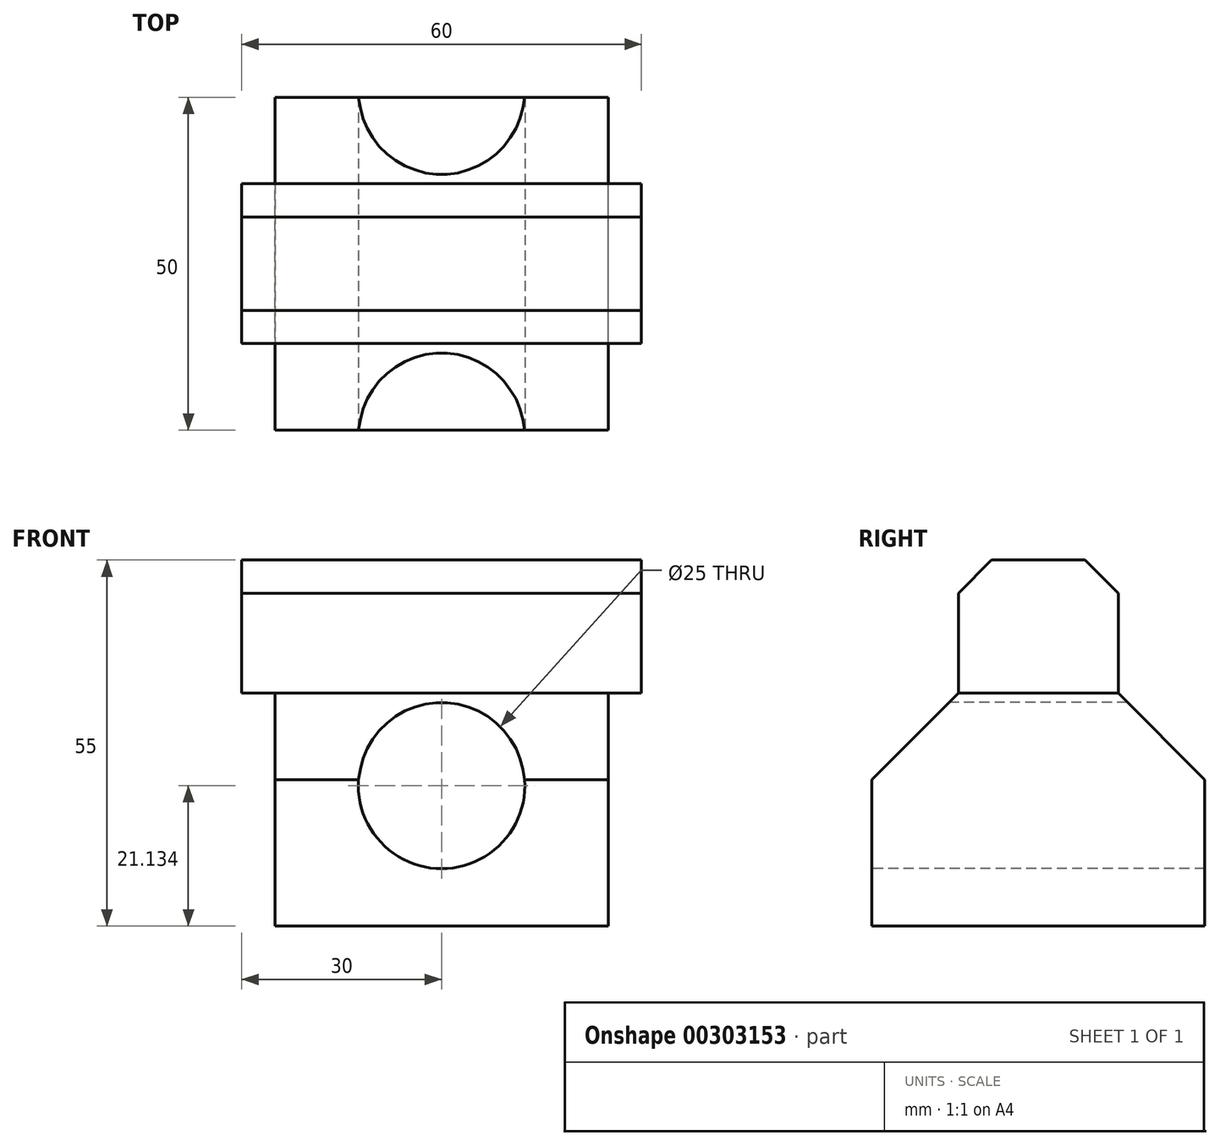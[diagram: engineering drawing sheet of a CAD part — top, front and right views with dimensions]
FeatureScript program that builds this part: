
annotation { "Feature Type Name" : "Feature", "Feature Type Description" : "" }
export const myFeature = defineFeature(function(context is Context, id is Id, definition is map)
    precondition{}
    {
        {
            var Q0;
            Q0=qCreatedBy(makeId("Top.planeOp"),FACE);
            var sketch = newSketch(context, id + "F0", { "sketchPlane" : qUnion([Q0])});
            skLineSegment(sketch, "E0.bottom", {"start": v(0, 0) * mm, "end": v(50, 0) * mm});
            skLineSegment(sketch, "E0.top", {"start": v(0, 50) * mm, "end": v(50, 50) * mm});
            skLineSegment(sketch, "E0.left", {"start": v(0, 0) * mm, "end": v(0, 50) * mm});
            skLineSegment(sketch, "E0.right", {"start": v(50, 0) * mm, "end": v(50, 50) * mm});
            skSolve(sketch);
        }
        {
            var Q0;
            Q0 = qSketchRegion(id + "F0", true);
            extrude(context, id + "F1", {"entities" : qUnion([Q0]), "depth" : 35 * mm});
        }
        {
            var Q0;
            Q0=makeQuery(id+"F1.opExtrude","SWEPT_FACE",FACE,{"disambiguationData":[OSD([sQuery(id+"F0.wireOp",EDGE,"E0.bottom")])]});
            var sketch = newSketch(context, id + "F2", { "sketchPlane" : qUnion([Q0])});
            skCircle(sketch, "E1", {"center": v(25, 21.13) * mm, "radius": 12.5 * mm});
            skPoint(sketch, "E1.centerSnap0", {"position": v(25, 35) * mm});
            skSolve(sketch);
        }
        {
            var Q0;
            Q0=sQuery(id+"F2.wireOp",VERTEX,"E1.center");
            var Q1;
            Q1=makeQuery(id+"F1.opExtrude","SWEPT_BODY",BODY,{"disambiguationData":[OSD([sQuery(id+"F0.wireOp",EDGE,"E0.bottom"),sQuery(id+"F0.wireOp",EDGE,"E0.top"),sQuery(id+"F0.wireOp",EDGE,"E0.left"),sQuery(id+"F0.wireOp",EDGE,"E0.right")])]});
            hole(context, id + "F3", {"style" : HoleStyle.SIMPLE, "endStyle" : HoleEndStyle.THROUGH, "holeDiameter" : 25 * mm, "tappedDepth" : 12 * mm, "tapClearance" : 3, "locations" : qUnion([Q0]), "scope" : qUnion([Q1])});
        }
        {
            var Q0;
            Q0=makeQuery(id+"F1.opExtrude","CAP_EDGE",EDGE,{"disambiguationData":[OSD([sQuery(id+"F0.wireOp",EDGE,"E0.bottom")])],"isStart":false});
            chamfer(context, id + "F4", {"entities" : qUnion([Q0]), "width" : 13 * mm, "tangentPropagation" : true});
        }
        {
            var Q0;
            Q0=makeQuery(id+"F1.opExtrude","CAP_EDGE",EDGE,{"disambiguationData":[OSD([sQuery(id+"F0.wireOp",EDGE,"E0.top")])],"isStart":false});
            chamfer(context, id + "F5", {"entities" : qUnion([Q0]), "width" : 13 * mm, "tangentPropagation" : true});
        }
        {
            var Q0;
            Q0=makeQuery(id+"F1.opExtrude","CAP_FACE",FACE,{"disambiguationData":[OSD([sQuery(id+"F0.wireOp",EDGE,"E0.bottom"),sQuery(id+"F0.wireOp",EDGE,"E0.top"),sQuery(id+"F0.wireOp",EDGE,"E0.left"),sQuery(id+"F0.wireOp",EDGE,"E0.right")])],"isStart":false});
            extrude(context, id + "F6", {"entities" : qUnion([Q0]), "operationType" : NewBodyOperationType.ADD, "depth" : 20 * mm});
        }
        {
            var Q0;
            {var subQ0=sQuery(id+"F0.wireOp",EDGE,"E0.right");var subQ1=sQuery(id+"F0.wireOp",EDGE,"E0.left");var subQ2=sQuery(id+"F0.wireOp",EDGE,"E0.top");var subQ3=sQuery(id+"F0.wireOp",EDGE,"E0.bottom");Q0=makeQuery(id+"F6.opExtrude","CAP_EDGE",EDGE,{"disambiguationData":[OSD([subQ3,subQ2,subQ1,subQ0]),TDD([makeQuery(id+"F5.opChamfer","BLEND_EDGE",EDGE,{"blendedFrom":[makeQuery(id+"F1.opExtrude","CAP_EDGE",EDGE,{"disambiguationData":[OSD([subQ2])],"isStart":false}),makeQuery(id+"F1.opExtrude","CAP_FACE",FACE,{"disambiguationData":[OSD([subQ3,subQ2,subQ1,subQ0])],"isStart":false})],"blendedInto":[makeQuery(id+"F1.opExtrude","CAP_FACE",FACE,{"disambiguationData":[OSD([subQ3,subQ2,subQ1,subQ0])],"isStart":false})]})])],"isStart":false});}
            chamfer(context, id + "F7", {"entities" : qUnion([Q0]), "width" : 5 * mm, "tangentPropagation" : true});
        }
        {
            var Q0;
            {var subQ0=sQuery(id+"F0.wireOp",EDGE,"E0.right");var subQ1=sQuery(id+"F0.wireOp",EDGE,"E0.left");var subQ2=sQuery(id+"F0.wireOp",EDGE,"E0.top");var subQ3=sQuery(id+"F0.wireOp",EDGE,"E0.bottom");Q0=makeQuery(id+"F6.opExtrude","CAP_EDGE",EDGE,{"disambiguationData":[OSD([subQ3,subQ2,subQ1,subQ0]),TDD([makeQuery(id+"F4.opChamfer","BLEND_EDGE",EDGE,{"blendedFrom":[makeQuery(id+"F1.opExtrude","CAP_EDGE",EDGE,{"disambiguationData":[OSD([subQ3])],"isStart":false}),makeQuery(id+"F1.opExtrude","CAP_FACE",FACE,{"disambiguationData":[OSD([subQ3,subQ2,subQ1,subQ0])],"isStart":false})],"blendedInto":[makeQuery(id+"F1.opExtrude","CAP_FACE",FACE,{"disambiguationData":[OSD([subQ3,subQ2,subQ1,subQ0])],"isStart":false})]})])],"isStart":false});}
            chamfer(context, id + "F8", {"entities" : qUnion([Q0]), "width" : 5 * mm, "tangentPropagation" : true});
        }
        {
            var Q0;
            {var subQ0=sQuery(id+"F0.wireOp",EDGE,"E0.right");Q0=makeQuery(id+"F6.boolean.opBoolean","MERGE",FACE,{"derivedFrom":[makeQuery(id+"F1.opExtrude","SWEPT_FACE",FACE,{"disambiguationData":[OSD([subQ0])]}),makeQuery(id+"F6.opExtrude","SWEPT_FACE",FACE,{"disambiguationData":[OSD([subQ0])]})]});}
            var sketch = newSketch(context, id + "F9", { "sketchPlane" : qUnion([Q0])});
            skLineSegment(sketch, "E2", {"start": v(13, 35) * mm, "end": v(37, 35) * mm});
            skSolve(sketch);
        }
        {
            var Q0;
            Q0=makeQuery(id+"F9.imprint","IMPRINT",FACE,{"disambiguationData":[TD([[makeQuery(id+"F9.imprint","IMPRINT",EDGE,{"derivedFrom":sQuery(id+"F9.wireOp",EDGE,"E2")}),1.0]])]});
            extrude(context, id + "F10", {"entities" : qUnion([Q0]), "operationType" : NewBodyOperationType.ADD, "depth" : 5 * mm});
        }
        {
            var Q0;
            {var subQ0=sQuery(id+"F0.wireOp",EDGE,"E0.left");Q0=makeQuery(id+"F6.boolean.opBoolean","MERGE",FACE,{"derivedFrom":[makeQuery(id+"F1.opExtrude","SWEPT_FACE",FACE,{"disambiguationData":[OSD([subQ0])]}),makeQuery(id+"F6.opExtrude","SWEPT_FACE",FACE,{"disambiguationData":[OSD([subQ0])]})]});}
            var sketch = newSketch(context, id + "F11", { "sketchPlane" : qUnion([Q0])});
            skLineSegment(sketch, "E3", {"start": v(-37, 35) * mm, "end": v(-13, 35) * mm});
            skSolve(sketch);
        }
        {
            var Q0;
            Q0=makeQuery(id+"F11.imprint","IMPRINT",FACE,{"disambiguationData":[TD([[makeQuery(id+"F11.imprint","IMPRINT",EDGE,{"derivedFrom":sQuery(id+"F11.wireOp",EDGE,"E3")}),1.0]])]});
            extrude(context, id + "F12", {"entities" : qUnion([Q0]), "operationType" : NewBodyOperationType.ADD, "depth" : 5 * mm});
        }
    });
